# Revit family: Valve-Box_ACUDOR_Recessed_ARVB
name_source: partatom
category: Doors
revit_build: Autodesk Revit 2017 (Build: 20171027_0315(x64)
units: mm (PartAtom-declared; Revit-internal decimal feet)

## family parameters
Cut with Voids When Loaded = No
Host = Face
Room Calculation Point = No
Shared = No

## types (6) — shared parameters
Analytic Construction = <None>
Default Elevation = 48 "
Description = RECESSED VALVE BOX
Manufacturer = ACUDOR
Material Finish = Metal - Acudor - Stainless - Polished
URL = www.acudor.com
zero-valued in all types: Wall Offset

## per-type parameters (varying)
| type | Height | Thickness | Width |
| ARVB-080804 | 9.62 " | 4 " | 9.62 " |
| ARVB-080806 | 9.62 " | 6 " | 9.62 " |
| ARVB-080808 | 9.62 " | 8 " | 9.62 " |
| ARVB-121204 | 13.62 " | 4 " | 13.62 " |
| ARVB-121206 | 13.62 " | 6 " | 13.62 " |
| ARVB-121208 | 13.62 " | 8 " | 13.62 " |

note: column(s) folded — value = type name in every type: Model

## geometry (parser evidence)
native form markers: Blend x2, Sweep x5
no freeform markers — native parametric forms only
